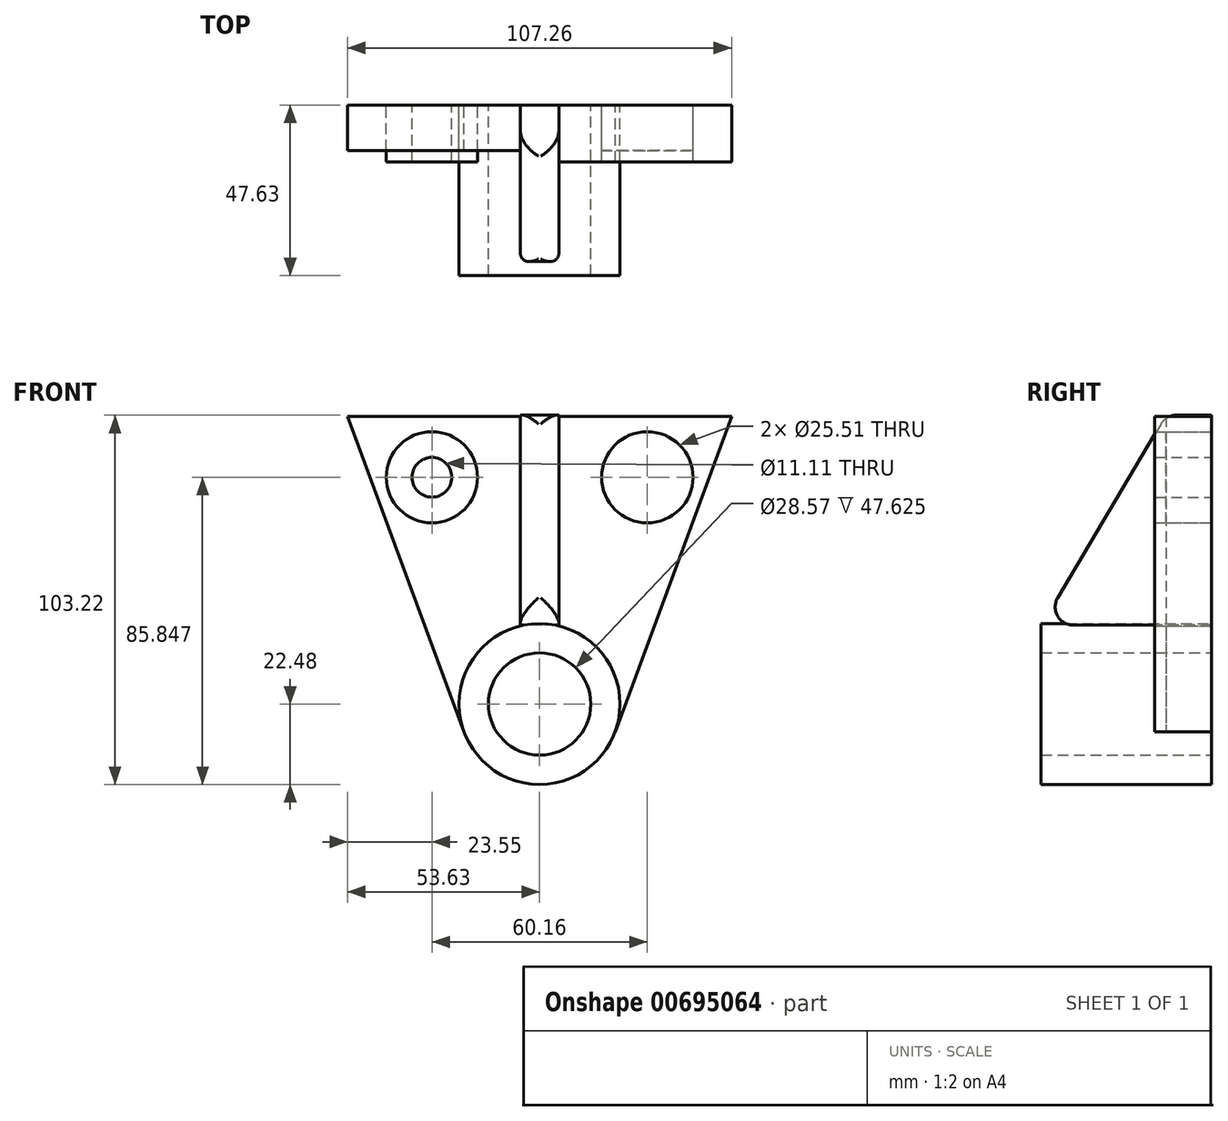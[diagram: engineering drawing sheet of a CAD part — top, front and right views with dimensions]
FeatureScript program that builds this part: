
annotation { "Feature Type Name" : "Feature", "Feature Type Description" : "" }
export const myFeature = defineFeature(function(context is Context, id is Id, definition is map)
    precondition{}
    {
        {
            var Q0;
            Q0=qCreatedBy(makeId("Front.planeOp"),FACE);
            var sketch = newSketch(context, id + "F0", { "sketchPlane" : qUnion([Q0])});
            skCircle(sketch, "E0", {"center": v(0, 0) * mm, "radius": 22.48 * mm});
            skCircle(sketch, "E1", {"center": v(-30.08, 63.37) * mm, "radius": 12.76 * mm});
            skCircle(sketch, "E2.MirrorC", {"center": v(30.08, 63.37) * mm, "radius": 12.76 * mm});
            skLineSegment(sketch, "E3", {"start": v(0, 80.43) * mm, "end": v(-53.63, 80.43) * mm});
            skLineSegment(sketch, "E4", {"start": v(-53.63, 80.43) * mm, "end": v(-19.77, -11.36) * mm});
            skLineSegment(sketch, "E5.MirrorCS", {"start": v(0, 80.43) * mm, "end": v(53.63, 80.43) * mm});
            skLineSegment(sketch, "E6.MirrorCS", {"start": v(53.63, 80.43) * mm, "end": v(19.77, -11.36) * mm});
            skPoint(sketch, "E7.orphan", {"position": v(0, 63.37) * mm});
            skLineSegment(sketch, "E8", {"start": v(0, 80.43) * mm, "end": v(5.37, 80.43) * mm});
            skLineSegment(sketch, "E9.MirrorCS", {"start": v(0, 80.43) * mm, "end": v(-5.37, 80.43) * mm});
            skLineSegment(sketch, "E10", {"start": v(-5.37, 80.43) * mm, "end": v(-5.37, 21.83) * mm});
            skLineSegment(sketch, "E11", {"start": v(5.37, 80.43) * mm, "end": v(5.37, 21.83) * mm});
            skSolve(sketch);
        }
        {
            var Q0;
            Q0=makeQuery(id+"F0.imprint","IMPRINT",FACE,{"disambiguationData":[TD([[makeQuery(id+"F0.imprint","IMPRINT",EDGE,{"derivedFrom":sQuery(id+"F0.wireOp",EDGE,"E1")}),-1.0]])]});
            var Q1;
            Q1=makeQuery(id+"F0.imprint","IMPRINT",FACE,{"disambiguationData":[TD([[makeQuery(id+"F0.imprint","IMPRINT",EDGE,{"derivedFrom":sQuery(id+"F0.wireOp",EDGE,"E2.MirrorC")}),1.0]])]});
            extrude(context, id + "F1", {"entities" : qUnion([Q0, Q1]), "depth" : 12.7 * mm, "offsetDistance" : 25.4 * mm});
        }
        {
            var Q0;
            Q0=makeQuery(id+"F0.imprint","IMPRINT",FACE,{"disambiguationData":[TD([[makeQuery(id+"F0.imprint","IMPRINT",EDGE,{"derivedFrom":sQuery(id+"F0.wireOp",EDGE,"E1")}),1.0]])]});
            var Q1;
            Q1=makeQuery(id+"F0.imprint","IMPRINT",FACE,{"disambiguationData":[TD([[makeQuery(id+"F0.imprint","IMPRINT",EDGE,{"derivedFrom":sQuery(id+"F0.wireOp",EDGE,"E2.MirrorC")}),-1.0]])]});
            extrude(context, id + "F2", {"entities" : qUnion([Q0, Q1]), "depth" : 15.88 * mm, "offsetDistance" : 25.4 * mm});
        }
        {
            var Q0;
            {var subQ0=sQuery(id+"F0.wireOp",EDGE,"E0");var subQ1=makeQuery(id+"F0.imprint","INTERSECT",VERTEX,{"derivedFrom":[subQ0,sQuery(id+"F0.wireOp",EDGE,"E10")]});Q0=makeQuery(id+"F0.imprint","IMPRINT",FACE,{"disambiguationData":[TD([[makeQuery(id+"F0.imprint","IMPRINT",EDGE,{"disambiguationData":[TD([[subQ1,1.0]])],"derivedFrom":subQ0}),1.0]])]});}
            extrude(context, id + "F3", {"entities" : qUnion([Q0]), "depth" : 47.62 * mm, "offsetDistance" : 25.4 * mm});
        }
        {
            var Q0;
            Q0=qCreatedBy(makeId("Right.planeOp"),FACE);
            var sketch = newSketch(context, id + "F4", { "sketchPlane" : qUnion([Q0])});
            skLineSegment(sketch, "E12", {"start": v(0, 22.04) * mm, "end": v(-47.55, 22.04) * mm});
            skLineSegment(sketch, "E13", {"start": v(0, 80.74) * mm, "end": v(-12.71, 80.74) * mm});
            skLineSegment(sketch, "E14", {"start": v(-12.71, 80.74) * mm, "end": v(-47.55, 22.04) * mm});
            skLineSegment(sketch, "E15", {"start": v(0, 80.74) * mm, "end": v(0, 22.04) * mm});
            skSolve(sketch);
        }
        {
            var Q0;
            Q0=makeQuery(id+"F4.imprint","IMPRINT",FACE,{"disambiguationData":[TD([[makeQuery(id+"F4.imprint","IMPRINT",EDGE,{"derivedFrom":sQuery(id+"F4.wireOp",EDGE,"E12")}),-1.0]])]});
            extrude(context, id + "F5", {"entities" : qUnion([Q0]), "depth" : 5.37 * mm, "offsetDistance" : 25.4 * mm, "hasSecondDirection" : true, "secondDirectionOppositeDirection" : true, "secondDirectionDepth" : 5.37 * mm});
        }
        {
            var Q0;
            Q0=sQuery(id+"F0.wireOp",VERTEX,"E1.center");
            var Q1;
            Q1=sQuery(id+"F0.wireOp",VERTEX,"E2.MirrorC.center");
            var Q2;
            Q2=makeQuery(id+"F2.opExtrude","SWEPT_BODY",BODY,{"disambiguationData":[OSD([sQuery(id+"F0.wireOp",EDGE,"E1")])]});
            var Q3;
            Q3=makeQuery(id+"F2.opExtrude","SWEPT_BODY",BODY,{"disambiguationData":[OSD([sQuery(id+"F0.wireOp",EDGE,"E2.MirrorC")])]});
            hole(context, id + "F6", {"style" : HoleStyle.SIMPLE, "endStyle" : HoleEndStyle.BLIND, "oppositeDirection" : true, "holeDiameter" : 11.1 * mm, "majorDiameter" : 6.35 * mm, "holeDepth" : 15.88 * mm, "isTappedThrough" : true, "tappedDepth" : 12.7 * mm, "tapClearance" : 3, "locations" : qUnion([Q0, Q1]), "scope" : qUnion([Q2, Q3])});
        }
        {
            var Q0;
            Q0=sQuery(id+"F0.wireOp",VERTEX,"E0.center");
            var Q1;
            Q1=makeQuery(id+"F3.opExtrude","SWEPT_BODY",BODY,{"disambiguationData":[OSD([sQuery(id+"F0.wireOp",EDGE,"E0")])]});
            hole(context, id + "F7", {"style" : HoleStyle.SIMPLE, "endStyle" : HoleEndStyle.BLIND, "oppositeDirection" : true, "holeDiameter" : 28.57 * mm, "majorDiameter" : 6.35 * mm, "holeDepth" : 47.62 * mm, "isTappedThrough" : true, "tappedDepth" : 12.7 * mm, "tapClearance" : 3, "locations" : qUnion([Q0]), "scope" : qUnion([Q1])});
        }
        {
            var Q0;
            Q0=makeQuery(id+"F5.opExtrude","SWEPT_FACE",FACE,{"disambiguationData":[OSD([sQuery(id+"F4.wireOp",EDGE,"E14")])]});
            fillet(context, id + "F8", {"entities" : qUnion([Q0]), "radius" : 5.08 * mm, "tangentPropagation" : true, "allowEdgeOverflow" : false});
        }
    });
